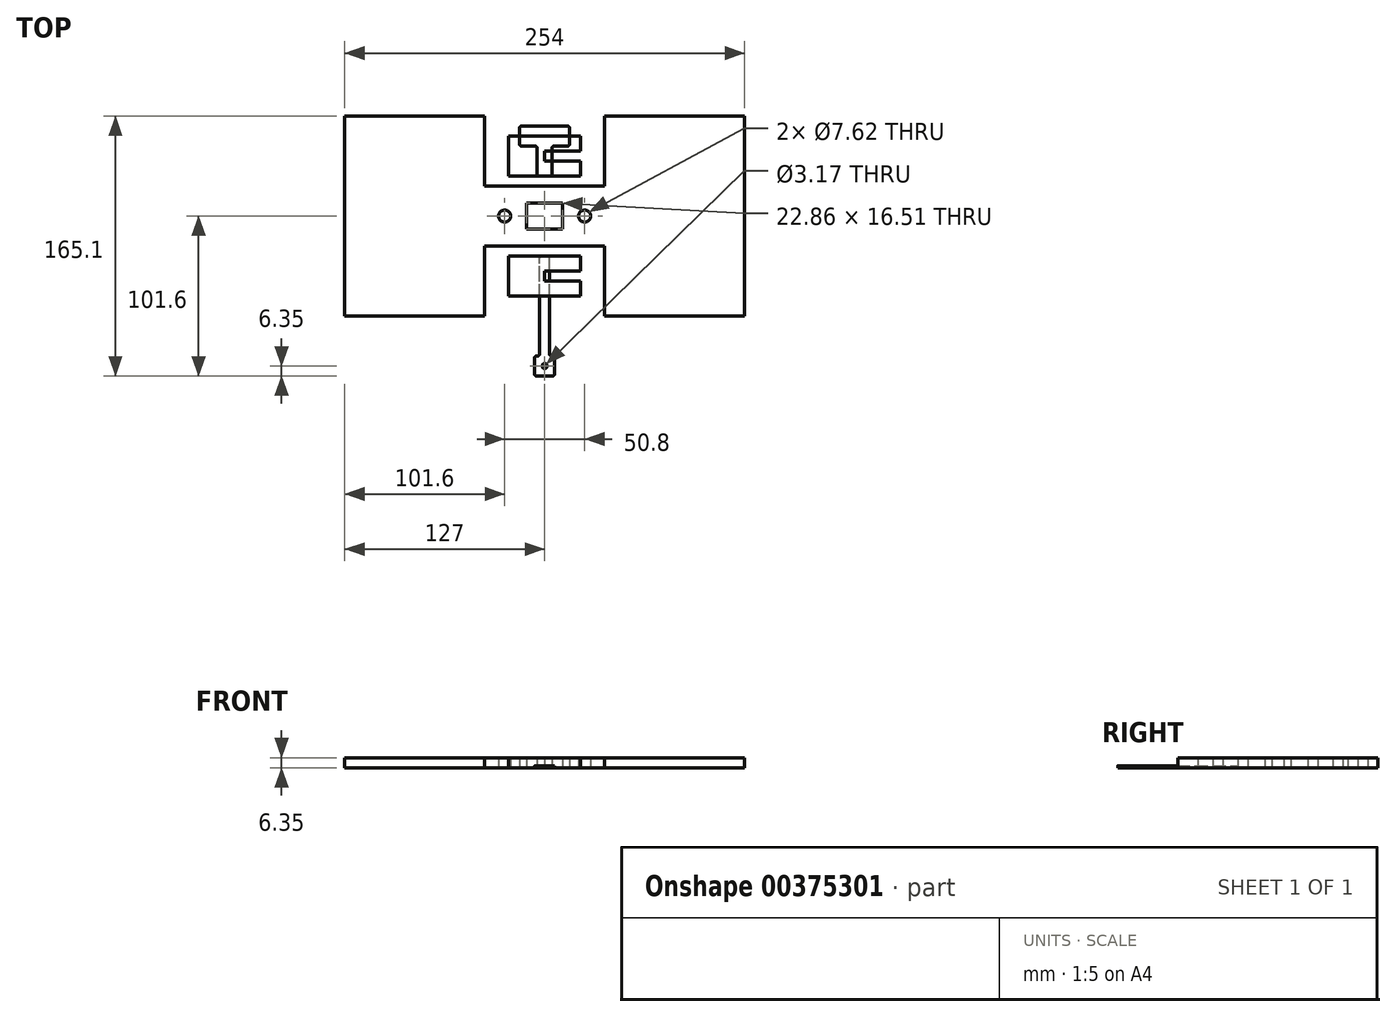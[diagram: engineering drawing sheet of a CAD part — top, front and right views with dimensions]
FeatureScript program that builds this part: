
annotation { "Feature Type Name" : "Feature", "Feature Type Description" : "" }
export const myFeature = defineFeature(function(context is Context, id is Id, definition is map)
    precondition{}
    {
        {
            var Q0;
            Q0=qCreatedBy(makeId("Top.planeOp"),FACE);
            var sketch = newSketch(context, id + "F0", { "sketchPlane" : qUnion([Q0])});
            skLineSegment(sketch, "E0.bottom", {"start": v(11.43, 8.26) * mm, "end": v(-11.43, 8.26) * mm});
            skLineSegment(sketch, "E0.top", {"start": v(11.43, -8.26) * mm, "end": v(-11.43, -8.26) * mm});
            skLineSegment(sketch, "E0.left", {"start": v(11.43, 8.26) * mm, "end": v(11.43, -8.26) * mm});
            skLineSegment(sketch, "E0.right", {"start": v(-11.43, 8.26) * mm, "end": v(-11.43, -8.26) * mm});
            skPoint(sketch, "E0.middle", {"position": v(0, 0) * mm});
            skCircle(sketch, "E1", {"center": v(-25.4, 0) * mm, "radius": 3.81 * mm});
            skCircle(sketch, "E2", {"center": v(25.4, 0) * mm, "radius": 3.81 * mm});
            skLineSegment(sketch, "E3", {"start": v(-25.4, 0) * mm, "end": v(0, 0) * mm, "construction": true});
            skLineSegment(sketch, "E4", {"start": v(0, 0) * mm, "end": v(25.4, 0) * mm, "construction": true});
            skLineSegment(sketch, "E5.bottom", {"start": v(127, 63.5) * mm, "end": v(38.1, 63.5) * mm});
            skLineSegment(sketch, "E5.top", {"start": v(127, -63.5) * mm, "end": v(38.1, -63.5) * mm});
            skLineSegment(sketch, "E5.left", {"start": v(127, 63.5) * mm, "end": v(127, -63.5) * mm});
            skLineSegment(sketch, "E5.right", {"start": v(-127, 63.5) * mm, "end": v(-127, -63.5) * mm});
            skLineSegment(sketch, "E6.top", {"start": v(38.1, -19.05) * mm, "end": v(-38.1, -19.05) * mm});
            skLineSegment(sketch, "E6.left", {"start": v(38.1, -57.15) * mm, "end": v(38.1, -19.05) * mm});
            skLineSegment(sketch, "E6.right", {"start": v(-38.1, -57.15) * mm, "end": v(-38.1, -19.05) * mm});
            skPoint(sketch, "E6.middle", {"position": v(0, -38.1) * mm});
            skLineSegment(sketch, "E7.bottom", {"start": v(22.86, -25.4) * mm, "end": v(-22.86, -25.4) * mm});
            skLineSegment(sketch, "E7.top", {"start": v(22.86, -50.8) * mm, "end": v(-22.86, -50.8) * mm});
            skLineSegment(sketch, "E7.left", {"start": v(22.86, -25.4) * mm, "end": v(22.86, -34.93) * mm});
            skLineSegment(sketch, "E7.right", {"start": v(-22.86, -25.4) * mm, "end": v(-22.86, -50.8) * mm});
            skLineSegment(sketch, "E8.bottom", {"start": v(22.86, -34.93) * mm, "end": v(0, -34.93) * mm});
            skLineSegment(sketch, "E8.top", {"start": v(22.86, -41.27) * mm, "end": v(0, -41.27) * mm});
            skLineSegment(sketch, "E8.right", {"start": v(0, -34.92) * mm, "end": v(0, -41.28) * mm});
            skLineSegment(sketch, "E9.trimOffspring", {"start": v(22.86, -41.27) * mm, "end": v(22.86, -50.8) * mm});
            skLineSegment(sketch, "E10.MirrorCS", {"start": v(0, 34.92) * mm, "end": v(0, 41.28) * mm});
            skPoint(sketch, "E11.MirrorP", {"position": v(0, 38.1) * mm});
            skLineSegment(sketch, "E12.MirrorCS", {"start": v(22.86, 25.4) * mm, "end": v(-22.86, 25.4) * mm});
            skLineSegment(sketch, "E13.MirrorCS", {"start": v(22.86, 41.27) * mm, "end": v(0, 41.27) * mm});
            skLineSegment(sketch, "E14.MirrorCS", {"start": v(22.86, 25.4) * mm, "end": v(22.86, 34.93) * mm});
            skLineSegment(sketch, "E15.MirrorCS", {"start": v(-22.86, 25.4) * mm, "end": v(-22.86, 50.8) * mm});
            skLineSegment(sketch, "E16.MirrorCS", {"start": v(38.1, 19.05) * mm, "end": v(-38.1, 19.05) * mm});
            skLineSegment(sketch, "E17.MirrorCS", {"start": v(22.86, 50.8) * mm, "end": v(-22.86, 50.8) * mm});
            skLineSegment(sketch, "E18.MirrorCS", {"start": v(38.1, 57.15) * mm, "end": v(38.1, 19.05) * mm});
            skLineSegment(sketch, "E19.MirrorCS", {"start": v(-38.1, 57.15) * mm, "end": v(-38.1, 19.05) * mm});
            skLineSegment(sketch, "E20.MirrorCS", {"start": v(22.86, 34.93) * mm, "end": v(0, 34.93) * mm});
            skLineSegment(sketch, "E21.MirrorCS", {"start": v(22.86, 41.27) * mm, "end": v(22.86, 50.8) * mm});
            skLineSegment(sketch, "E22", {"start": v(-38.1, -57.15) * mm, "end": v(-38.1, -63.5) * mm});
            skLineSegment(sketch, "E23", {"start": v(38.1, -57.15) * mm, "end": v(38.1, -63.5) * mm});
            skLineSegment(sketch, "E24.trimOffspring", {"start": v(-38.1, -63.5) * mm, "end": v(-127, -63.5) * mm});
            skLineSegment(sketch, "E25", {"start": v(-38.1, 57.15) * mm, "end": v(-38.1, 63.5) * mm});
            skLineSegment(sketch, "E26", {"start": v(38.1, 57.15) * mm, "end": v(38.1, 63.5) * mm});
            skLineSegment(sketch, "E27.trimOffspring", {"start": v(-38.1, 63.5) * mm, "end": v(-127, 63.5) * mm});
            skSolve(sketch);
        }
        {
            var Q0;
            Q0 = qSketchRegion(id + "F0", true);
            extrude(context, id + "F1", {"entities" : qUnion([Q0]), "depth" : 6.35 * mm, "offsetDistance" : 25.4 * mm});
        }
        {
            var Q0;
            Q0=qCreatedBy(makeId("Top.planeOp"),FACE);
            var sketch = newSketch(context, id + "F2", { "sketchPlane" : qUnion([Q0])});
            skLineSegment(sketch, "E28.bottom", {"start": v(14.6, 44.45) * mm, "end": v(6.03, 44.45) * mm});
            skLineSegment(sketch, "E28.top", {"start": v(14.6, 57.15) * mm, "end": v(-14.6, 57.15) * mm});
            skLineSegment(sketch, "E28.left", {"start": v(15.87, 45.72) * mm, "end": v(15.87, 55.88) * mm});
            skLineSegment(sketch, "E28.right", {"start": v(-15.88, 45.72) * mm, "end": v(-15.88, 55.88) * mm});
            skPoint(sketch, "E28.middle", {"position": v(0, 50.8) * mm});
            skLineSegment(sketch, "E29.bottom", {"start": v(3.5, 25.4) * mm, "end": v(-3.5, 25.4) * mm});
            skLineSegment(sketch, "E29.left", {"start": v(4.76, 26.67) * mm, "end": v(4.76, 43.18) * mm});
            skLineSegment(sketch, "E29.right", {"start": v(-4.76, 26.67) * mm, "end": v(-4.76, 43.18) * mm});
            skPoint(sketch, "E29.middle", {"position": v(0, 34.93) * mm});
            skPoint(sketch, "E29.middle.positionSnap0", {"position": v(0, 44.45) * mm});
            skPoint(sketch, "E29.centerSnap0", {"position": v(0, 44.45) * mm});
            skLineSegment(sketch, "E30.top", {"start": v(1.9, -25.4) * mm, "end": v(-1.9, -25.4) * mm});
            skLineSegment(sketch, "E30.left", {"start": v(3.18, -87.63) * mm, "end": v(3.18, -26.67) * mm});
            skLineSegment(sketch, "E30.right", {"start": v(-3.17, -87.63) * mm, "end": v(-3.17, -26.67) * mm});
            skPoint(sketch, "E30.middle", {"position": v(0, -57.15) * mm});
            skLineSegment(sketch, "E31.bottom", {"start": v(5.08, -101.6) * mm, "end": v(-5.08, -101.6) * mm});
            skLineSegment(sketch, "E31.left", {"start": v(6.35, -100.33) * mm, "end": v(6.35, -90.17) * mm});
            skLineSegment(sketch, "E31.right", {"start": v(-6.35, -100.33) * mm, "end": v(-6.35, -90.17) * mm});
            skPoint(sketch, "E31.middle", {"position": v(0, -95.25) * mm});
            skCircle(sketch, "E32", {"center": v(0, -95.25) * mm, "radius": 1.59 * mm});
            skLineSegment(sketch, "E33.trimOffspring", {"start": v(-6.03, 44.45) * mm, "end": v(-14.6, 44.45) * mm});
            skLineSegment(sketch, "E34.trimOffspring", {"start": v(-4.44, -88.9) * mm, "end": v(-5.08, -88.9) * mm});
            skPoint(sketch, "E35", {"position": v(0, -25.4) * mm});
            skPoint(sketch, "E36", {"position": v(0, 25.4) * mm});
            skLineSegment(sketch, "E37", {"start": v(4.45, -88.9) * mm, "end": v(5.08, -88.9) * mm});
            skPoint(sketch, "E38.visualSharp", {"position": v(-6.35, -101.6) * mm});
            skArc(sketch, "E38.filletArc", {"start": v(-6.35, -100.33) * mm, "mid": v(-5.98, -101.23) * mm, "end": v(-5.08, -101.6) * mm});
            skPoint(sketch, "E39.visualSharp", {"position": v(6.35, -101.6) * mm});
            skArc(sketch, "E39.filletArc", {"start": v(5.08, -101.6) * mm, "mid": v(5.98, -101.23) * mm, "end": v(6.35, -100.33) * mm});
            skPoint(sketch, "E40.visualSharp", {"position": v(-6.35, -88.9) * mm});
            skArc(sketch, "E40.filletArc", {"start": v(-5.08, -88.9) * mm, "mid": v(-5.98, -89.27) * mm, "end": v(-6.35, -90.17) * mm});
            skPoint(sketch, "E41.visualSharp", {"position": v(6.35, -88.9) * mm});
            skArc(sketch, "E41.filletArc", {"start": v(6.35, -90.17) * mm, "mid": v(5.98, -89.27) * mm, "end": v(5.08, -88.9) * mm});
            skPoint(sketch, "E42.visualSharp", {"position": v(-3.17, -25.4) * mm});
            skArc(sketch, "E42.filletArc", {"start": v(-1.9, -25.4) * mm, "mid": v(-2.8, -25.77) * mm, "end": v(-3.17, -26.67) * mm});
            skPoint(sketch, "E43.visualSharp", {"position": v(3.18, -25.4) * mm});
            skArc(sketch, "E43.filletArc", {"start": v(3.18, -26.67) * mm, "mid": v(2.8, -25.77) * mm, "end": v(1.9, -25.4) * mm});
            skPoint(sketch, "E44.visualSharp", {"position": v(-3.17, -88.9) * mm});
            skArc(sketch, "E44.filletArc", {"start": v(-4.44, -88.9) * mm, "mid": v(-3.55, -88.53) * mm, "end": v(-3.17, -87.63) * mm});
            skPoint(sketch, "E45.visualSharp", {"position": v(3.18, -88.9) * mm});
            skArc(sketch, "E45.filletArc", {"start": v(3.18, -87.63) * mm, "mid": v(3.55, -88.53) * mm, "end": v(4.45, -88.9) * mm});
            skPoint(sketch, "E46.visualSharp", {"position": v(-4.76, 25.4) * mm});
            skArc(sketch, "E46.filletArc", {"start": v(-4.76, 26.67) * mm, "mid": v(-4.4, 25.77) * mm, "end": v(-3.5, 25.4) * mm});
            skPoint(sketch, "E47.visualSharp", {"position": v(4.76, 25.4) * mm});
            skArc(sketch, "E47.filletArc", {"start": v(3.5, 25.4) * mm, "mid": v(4.4, 25.77) * mm, "end": v(4.76, 26.67) * mm});
            skPoint(sketch, "E48.visualSharp", {"position": v(4.76, 44.45) * mm});
            skArc(sketch, "E48.filletArc", {"start": v(6.03, 44.45) * mm, "mid": v(5.13, 44.08) * mm, "end": v(4.76, 43.18) * mm});
            skPoint(sketch, "E49.visualSharp", {"position": v(15.88, 44.45) * mm});
            skArc(sketch, "E49.filletArc", {"start": v(14.6, 44.45) * mm, "mid": v(15.5, 44.82) * mm, "end": v(15.88, 45.72) * mm});
            skPoint(sketch, "E50.visualSharp", {"position": v(15.88, 57.15) * mm});
            skArc(sketch, "E50.filletArc", {"start": v(15.87, 55.88) * mm, "mid": v(15.5, 56.78) * mm, "end": v(14.6, 57.15) * mm});
            skPoint(sketch, "E51.visualSharp", {"position": v(-4.76, 44.45) * mm});
            skArc(sketch, "E51.filletArc", {"start": v(-4.76, 43.18) * mm, "mid": v(-5.13, 44.08) * mm, "end": v(-6.03, 44.45) * mm});
            skPoint(sketch, "E52.visualSharp", {"position": v(-15.88, 44.45) * mm});
            skArc(sketch, "E52.filletArc", {"start": v(-15.88, 45.72) * mm, "mid": v(-15.5, 44.82) * mm, "end": v(-14.6, 44.45) * mm});
            skPoint(sketch, "E53.visualSharp", {"position": v(-15.88, 57.15) * mm});
            skArc(sketch, "E53.filletArc", {"start": v(-14.6, 57.15) * mm, "mid": v(-15.5, 56.78) * mm, "end": v(-15.88, 55.88) * mm});
            skSolve(sketch);
        }
        {
            var Q0;
            Q0=makeQuery(id+"F2.imprint","IMPRINT",FACE,{"disambiguationData":[TD([[makeQuery(id+"F2.imprint","IMPRINT",EDGE,{"derivedFrom":sQuery(id+"F2.wireOp",EDGE,"E28.bottom")}),-1.0]])]});
            extrude(context, id + "F3", {"entities" : qUnion([Q0]), "depth" : 6.35 * mm, "offsetDistance" : 25.4 * mm});
        }
        {
            var Q0;
            Q0=makeQuery(id+"F2.imprint","IMPRINT",FACE,{"disambiguationData":[TD([[makeQuery(id+"F2.imprint","IMPRINT",EDGE,{"derivedFrom":sQuery(id+"F2.wireOp",EDGE,"E30.top")}),1.0]])]});
            extrude(context, id + "F4", {"entities" : qUnion([Q0]), "depth" : 1.27 * mm, "offsetDistance" : 25.4 * mm});
        }
    });
